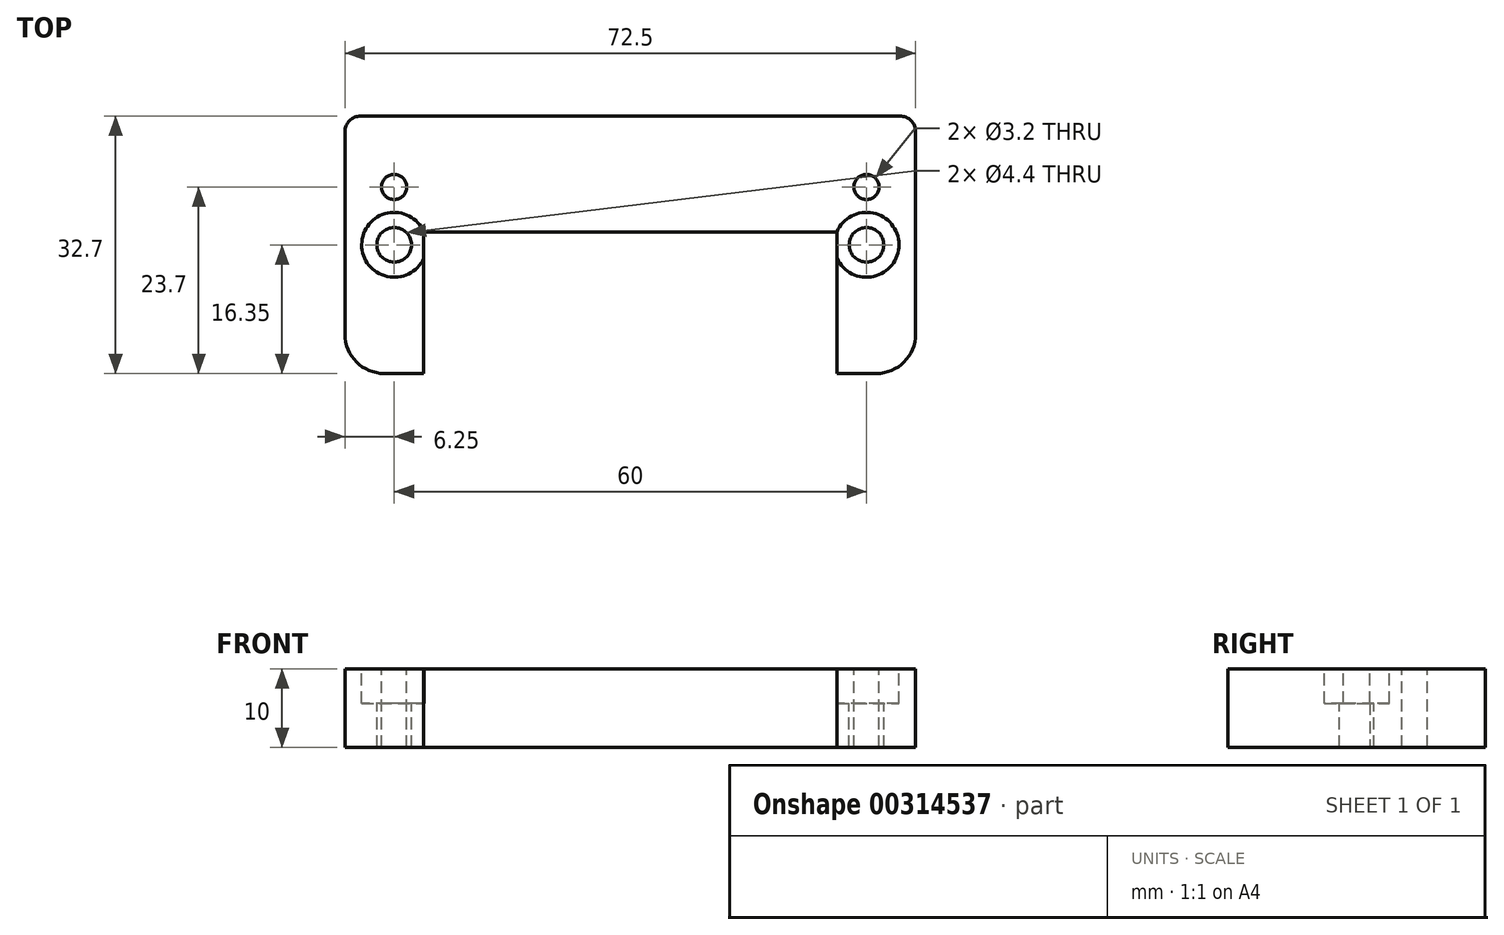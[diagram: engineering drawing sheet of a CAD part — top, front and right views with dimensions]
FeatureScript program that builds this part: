
annotation { "Feature Type Name" : "Feature", "Feature Type Description" : "" }
export const myFeature = defineFeature(function(context is Context, id is Id, definition is map)
    precondition{}
    {
        {
            var Q0;
            Q0=qCreatedBy(makeId("Top.planeOp"),FACE);
            var sketch = newSketch(context, id + "F0", { "sketchPlane" : qUnion([Q0])});
            skLineSegment(sketch, "E0.bottom", {"start": v(-36.25, -16.35) * mm, "end": v(-26.25, -16.35) * mm});
            skLineSegment(sketch, "E0.top", {"start": v(-36.25, 16.35) * mm, "end": v(36.25, 16.35) * mm});
            skLineSegment(sketch, "E0.left", {"start": v(-36.25, -16.35) * mm, "end": v(-36.25, 16.35) * mm});
            skLineSegment(sketch, "E0.right", {"start": v(36.25, -16.35) * mm, "end": v(36.25, 16.35) * mm});
            skPoint(sketch, "E0.middle", {"position": v(0, 0) * mm});
            skLineSegment(sketch, "E1.top", {"start": v(-26.25, 1.65) * mm, "end": v(26.25, 1.65) * mm});
            skLineSegment(sketch, "E1.left", {"start": v(-26.25, -16.35) * mm, "end": v(-26.25, 1.65) * mm});
            skLineSegment(sketch, "E1.right", {"start": v(26.25, -16.35) * mm, "end": v(26.25, 1.65) * mm});
            skLineSegment(sketch, "E2.trimOffspring", {"start": v(26.25, -16.35) * mm, "end": v(36.25, -16.35) * mm});
            skSolve(sketch);
        }
        {
            var Q0;
            Q0=qSketchRegion(id+"F0",true);
            extrude(context, id + "F1", {"entities" : qUnion([Q0]), "depth" : 10 * mm});
        }
        {
            var Q0;
            Q0=makeQuery(id+"F1.opExtrude","CAP_FACE",FACE,{"disambiguationData":[OSD([sQuery(id+"F0.wireOp",EDGE,"E0.bottom"),sQuery(id+"F0.wireOp",EDGE,"E0.top"),sQuery(id+"F0.wireOp",EDGE,"E0.left"),sQuery(id+"F0.wireOp",EDGE,"E0.right"),sQuery(id+"F0.wireOp",EDGE,"E1.top"),sQuery(id+"F0.wireOp",EDGE,"E1.left"),sQuery(id+"F0.wireOp",EDGE,"E1.right"),sQuery(id+"F0.wireOp",EDGE,"E2.trimOffspring")])],"isStart":false});
            var sketch = newSketch(context, id + "F2", { "sketchPlane" : qUnion([Q0])});
            skPoint(sketch, "E3", {"position": v(-30, 7.35) * mm});
            skPoint(sketch, "E4.1.0.0", {"position": v(30, 7.35) * mm});
            skLineSegment(sketch, "E4.direction1", {"start": v(-30, 7.35) * mm, "end": v(30, 7.35) * mm, "construction": true});
            skSolve(sketch);
        }
        {
            var Q0;
            Q0=sQuery(id+"F2.wireOp",VERTEX,"E3");
            var Q1;
            Q1=sQuery(id+"F2.wireOp",VERTEX,"E4.1.0.0");
            var Q2;
            Q2=makeQuery(id+"F1.opExtrude","SWEPT_BODY",BODY,{"disambiguationData":[OSD([sQuery(id+"F0.wireOp",EDGE,"E0.bottom"),sQuery(id+"F0.wireOp",EDGE,"E0.top"),sQuery(id+"F0.wireOp",EDGE,"E0.left"),sQuery(id+"F0.wireOp",EDGE,"E0.right"),sQuery(id+"F0.wireOp",EDGE,"E1.top"),sQuery(id+"F0.wireOp",EDGE,"E1.left"),sQuery(id+"F0.wireOp",EDGE,"E1.right"),sQuery(id+"F0.wireOp",EDGE,"E2.trimOffspring")])]});
            hole(context, id + "F3", {"style" : HoleStyle.SIMPLE, "endStyle" : HoleEndStyle.BLIND, "standardTappedOrClearance" : lookupTablePath({ "standard" : "ISO", "engagement" : "75%", "pitch" : "0.75 mm", "size" : "M4", "type" : "Tapped" }), "standardBlindInLast" : lookupTablePath({ "standard" : "ISO", "engagement" : "75%", "pitch" : "0.75 mm", "size" : "M4", "type" : "Tapped" }), "holeDiameter" : 3.2 * mm, "showTappedDepth" : true, "holeDepth" : 14.25 * mm, "tappedDepth" : 12 * mm, "tapClearance" : 3, "locations" : qUnion([Q0, Q1]), "scope" : qUnion([Q2])});
        }
        {
            var Q0;
            Q0=makeQuery(id+"F1.opExtrude","SWEPT_EDGE",EDGE,{"disambiguationData":[OSD([sQuery(id+"F0.wireOp",EDGE,"E0.bottom"),sQuery(id+"F0.wireOp",EDGE,"E0.left")])]});
            var Q1;
            Q1=makeQuery(id+"F1.opExtrude","SWEPT_EDGE",EDGE,{"disambiguationData":[OSD([sQuery(id+"F0.wireOp",EDGE,"E0.right"),sQuery(id+"F0.wireOp",EDGE,"E2.trimOffspring")])]});
            fillet(context, id + "F4", {"entities" : qUnion([Q0, Q1]), "radius" : 5 * mm, "tangentPropagation" : true, "allowEdgeOverflow" : false});
        }
        {
            var Q0;
            Q0=makeQuery(id+"F1.opExtrude","SWEPT_EDGE",EDGE,{"disambiguationData":[OSD([sQuery(id+"F0.wireOp",EDGE,"E0.top"),sQuery(id+"F0.wireOp",EDGE,"E0.right")])]});
            var Q1;
            Q1=makeQuery(id+"F1.opExtrude","SWEPT_EDGE",EDGE,{"disambiguationData":[OSD([sQuery(id+"F0.wireOp",EDGE,"E0.top"),sQuery(id+"F0.wireOp",EDGE,"E0.left")])]});
            fillet(context, id + "F5", {"entities" : qUnion([Q0, Q1]), "radius" : 2 * mm, "tangentPropagation" : true, "allowEdgeOverflow" : false});
        }
        {
            var Q0;
            Q0=makeQuery(id+"F1.opExtrude","CAP_FACE",FACE,{"disambiguationData":[OSD([sQuery(id+"F0.wireOp",EDGE,"E0.bottom"),sQuery(id+"F0.wireOp",EDGE,"E0.top"),sQuery(id+"F0.wireOp",EDGE,"E0.left"),sQuery(id+"F0.wireOp",EDGE,"E0.right"),sQuery(id+"F0.wireOp",EDGE,"E1.top"),sQuery(id+"F0.wireOp",EDGE,"E1.left"),sQuery(id+"F0.wireOp",EDGE,"E1.right"),sQuery(id+"F0.wireOp",EDGE,"E2.trimOffspring")])],"isStart":false});
            var sketch = newSketch(context, id + "F6", { "sketchPlane" : qUnion([Q0])});
            skLineSegment(sketch, "E5", {"start": v(-30, 7.35) * mm, "end": v(-30, -18.22) * mm, "construction": true});
            skPoint(sketch, "E6", {"position": v(-30, 0) * mm});
            skPoint(sketch, "E7.MirrorP", {"position": v(30, 0) * mm});
            skSolve(sketch);
        }
        {
            var Q0;
            Q0=sQuery(id+"F6.wireOp",VERTEX,"E6");
            var Q1;
            Q1=sQuery(id+"F6.wireOp",VERTEX,"E7.MirrorP");
            var Q2;
            Q2=makeQuery(id+"F1.opExtrude","SWEPT_BODY",BODY,{"disambiguationData":[OSD([sQuery(id+"F0.wireOp",EDGE,"E0.bottom"),sQuery(id+"F0.wireOp",EDGE,"E0.top"),sQuery(id+"F0.wireOp",EDGE,"E0.left"),sQuery(id+"F0.wireOp",EDGE,"E0.right"),sQuery(id+"F0.wireOp",EDGE,"E1.top"),sQuery(id+"F0.wireOp",EDGE,"E1.left"),sQuery(id+"F0.wireOp",EDGE,"E1.right"),sQuery(id+"F0.wireOp",EDGE,"E2.trimOffspring")])]});
            hole(context, id + "F7", {"style" : HoleStyle.C_BORE, "endStyle" : HoleEndStyle.THROUGH, "holeDiameter" : 4.4 * mm, "cBoreDiameter" : 8.25 * mm, "cBoreDepth" : 4.4 * mm, "isTappedThrough" : true, "tappedDepth" : 12 * mm, "tapClearance" : 3, "locations" : qUnion([Q0, Q1]), "scope" : qUnion([Q2])});
        }
    });
